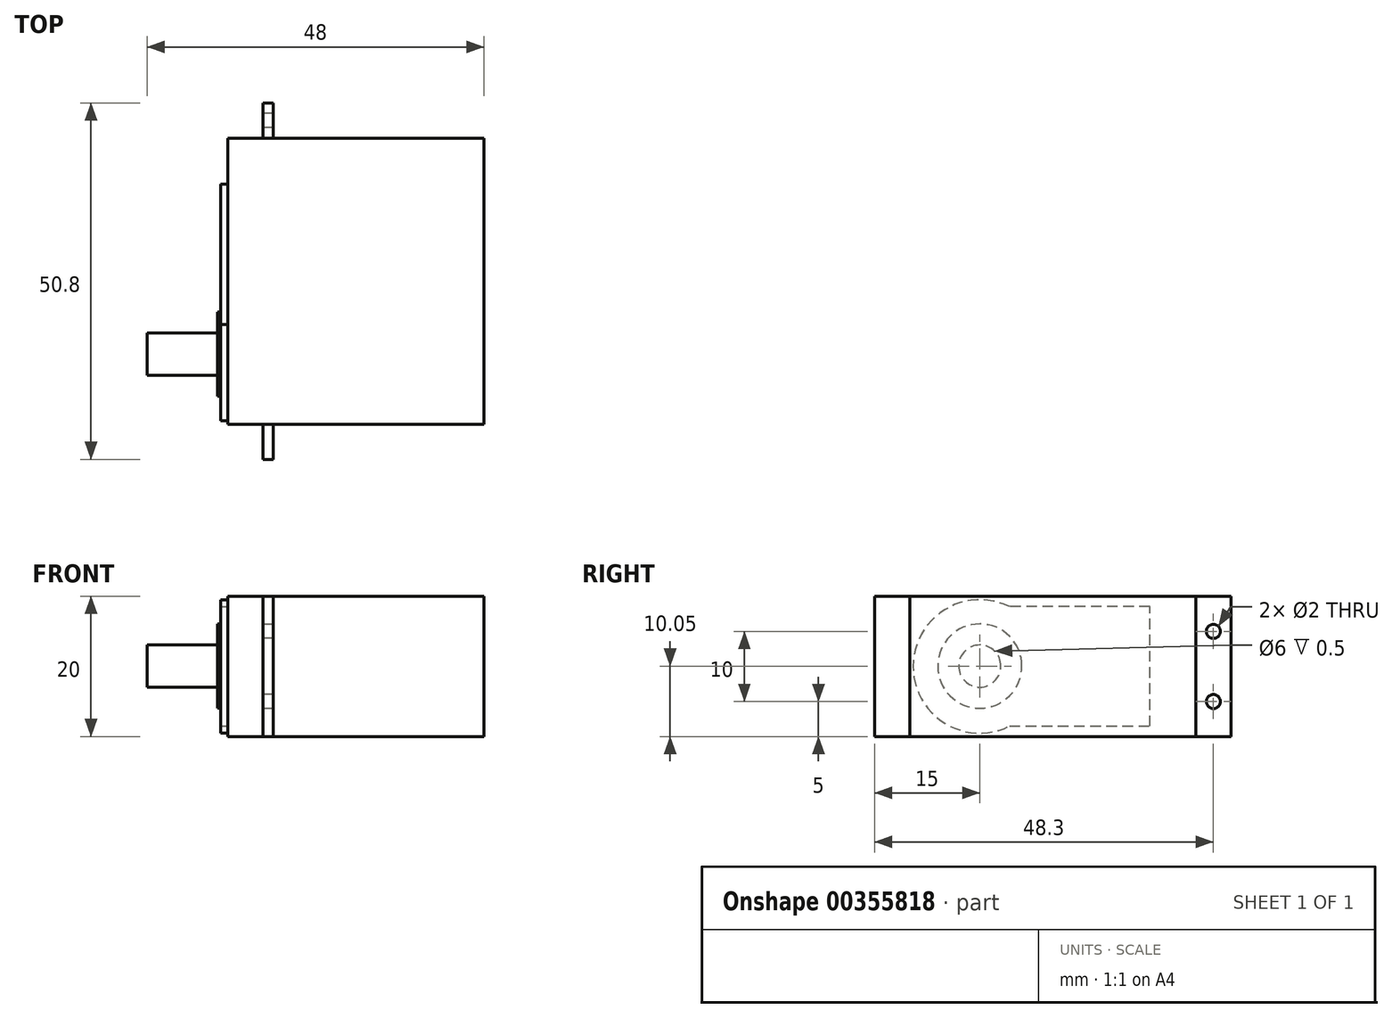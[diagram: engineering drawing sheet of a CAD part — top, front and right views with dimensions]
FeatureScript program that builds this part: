
annotation { "Feature Type Name" : "Feature", "Feature Type Description" : "" }
export const myFeature = defineFeature(function(context is Context, id is Id, definition is map)
    precondition{}
    {
        {
            var Q0;
            Q0=qCreatedBy(makeId("Front.planeOp"),FACE);
            var sketch = newSketch(context, id + "F0", { "sketchPlane" : qUnion([Q0])});
            skLineSegment(sketch, "E0.bottom", {"start": v(0, 0) * mm, "end": v(36.5, 0) * mm});
            skLineSegment(sketch, "E0.top", {"start": v(0, 20) * mm, "end": v(36.5, 20) * mm});
            skLineSegment(sketch, "E0.left", {"start": v(0, 0) * mm, "end": v(0, 20) * mm});
            skLineSegment(sketch, "E0.right", {"start": v(36.5, 0) * mm, "end": v(36.5, 20) * mm});
            skSolve(sketch);
        }
        {
            var Q0;
            Q0=qSketchRegion(id+"F0",true);
            extrude(context, id + "F1", {"entities" : qUnion([Q0]), "endBound" : BoundingType.SYMMETRIC, "depth" : 40.8 * mm});
        }
        {
            var Q0;
            Q0=qCreatedBy(makeId("Right.planeOp"),FACE);
            cPlane(context, id + "F2", {"entities" : qUnion([Q0]), "cplaneType" : CPlaneType.OFFSET, "offset" : 5 * mm, "width" : 150 * mm, "height" : 150 * mm});
        }
        {
            var Q0;
            Q0=qCreatedBy(id+"F2.planeOp",FACE);
            var sketch = newSketch(context, id + "F3", { "sketchPlane" : qUnion([Q0])});
            skLineSegment(sketch, "E1.0", {"start": v(-20.4, 0) * mm, "end": v(-20.4, 20) * mm});
            skLineSegment(sketch, "E2", {"start": v(-20.4, 0) * mm, "end": v(-25.4, 0) * mm});
            skLineSegment(sketch, "E3", {"start": v(-25.4, 0) * mm, "end": v(-25.4, 20) * mm});
            skLineSegment(sketch, "E4", {"start": v(-25.4, 20) * mm, "end": v(-20.4, 20) * mm});
            skSolve(sketch);
        }
        {
            var Q0;
            Q0=qSketchRegion(id+"F3",true);
            extrude(context, id + "F4", {"entities" : qUnion([Q0]), "depth" : 1.5 * mm});
        }
        {
            var Q0;
            Q0=makeQuery(id+"F4.opExtrude","SWEPT_BODY",BODY,{"disambiguationData":[OSD([sQuery(id+"F3.wireOp",EDGE,"E1.0"),sQuery(id+"F3.wireOp",EDGE,"E2"),sQuery(id+"F3.wireOp",EDGE,"E3"),sQuery(id+"F3.wireOp",EDGE,"E4")])]});
            var Q1;
            Q1=qCreatedBy(makeId("Front.planeOp"),FACE);
            mirror(context, id + "F5", {"entities" : qUnion([Q0]), "mirrorPlane" : qUnion([Q1])});
        }
        {
            var Q0;
            Q0=makeQuery(id+"F1.opExtrude","SWEPT_FACE",FACE,{"disambiguationData":[OSD([sQuery(id+"F0.wireOp",EDGE,"E0.left")])]});
            var sketch = newSketch(context, id + "F6", { "sketchPlane" : qUnion([Q0])});
            skArc(sketch, "E5", {"start": v(6.16, 1.5) * mm, "mid": v(19.9, 10) * mm, "end": v(6.16, 18.5) * mm});
            skPoint(sketch, "E5.centerSnap0", {"position": v(20.4, 10) * mm});
            skLineSegment(sketch, "E6", {"start": v(6.16, 1.5) * mm, "end": v(-13.84, 1.5) * mm});
            skLineSegment(sketch, "E7", {"start": v(-13.84, 1.5) * mm, "end": v(-13.84, 18.5) * mm});
            skLineSegment(sketch, "E8", {"start": v(-13.84, 18.5) * mm, "end": v(6.16, 18.5) * mm});
            skLineSegment(sketch, "E9", {"start": v(-45.44, 10) * mm, "end": v(35.03, 10) * mm, "construction": true});
            skPoint(sketch, "E9.startSnap0", {"position": v(-20.4, 10) * mm});
            skSolve(sketch);
        }
        {
            var Q0;
            Q0=qSketchRegion(id+"F6",true);
            extrude(context, id + "F7", {"entities" : qUnion([Q0]), "operationType" : NewBodyOperationType.ADD, "depth" : 1 * mm});
        }
        {
            var Q0;
            Q0=makeQuery(id+"F7.opExtrude","CAP_FACE",FACE,{"disambiguationData":[OSD([sQuery(id+"F6.wireOp",EDGE,"E5"),sQuery(id+"F6.wireOp",EDGE,"E6"),sQuery(id+"F6.wireOp",EDGE,"E7"),sQuery(id+"F6.wireOp",EDGE,"E8")])],"isStart":false});
            var sketch = newSketch(context, id + "F8", { "sketchPlane" : qUnion([Q0])});
            skCircle(sketch, "E10", {"center": v(10.4, 10.05) * mm, "radius": 6 * mm});
            skPoint(sketch, "E11.0.3.start.orphan", {"position": v(-13.84, 1.5) * mm});
            skPoint(sketch, "E11.0.1.end.orphan", {"position": v(-13.84, 18.5) * mm});
            skPoint(sketch, "E11.0.0.end.orphan", {"position": v(6.16, 18.5) * mm});
            skPoint(sketch, "E11.0.0.start.orphan", {"position": v(6.16, 1.5) * mm});
            skSolve(sketch);
        }
        {
            var Q0;
            Q0=qSketchRegion(id+"F8",true);
            extrude(context, id + "F9", {"entities" : qUnion([Q0]), "operationType" : NewBodyOperationType.ADD, "depth" : .5 * mm});
        }
        {
            var Q0;
            Q0=makeQuery(id+"F9.opExtrude","CAP_FACE",FACE,{"disambiguationData":[OSD([sQuery(id+"F8.wireOp",EDGE,"E10")])],"isStart":false});
            var sketch = newSketch(context, id + "F10", { "sketchPlane" : qUnion([Q0])});
            skCircle(sketch, "E12", {"center": v(10.4, 10.05) * mm, "radius": 3 * mm});
            skSolve(sketch);
        }
        {
            var Q0;
            Q0=qSketchRegion(id+"F10",true);
            extrude(context, id + "F11", {"entities" : qUnion([Q0]), "operationType" : NewBodyOperationType.REMOVE, "oppositeDirection" : true, "depth" : .5 * mm});
        }
        {
            var Q0;
            Q0=makeQuery(id+"F9.opExtrude","CAP_FACE",FACE,{"disambiguationData":[OSD([sQuery(id+"F8.wireOp",EDGE,"E10")])],"isStart":false});
            var sketch = newSketch(context, id + "F12", { "sketchPlane" : qUnion([Q0])});
            skCircle(sketch, "E13.0", {"center": v(10.4, 10.05) * mm, "radius": 3 * mm});
            skSolve(sketch);
        }
        {
            var Q0;
            Q0=qSketchRegion(id+"F12",true);
            extrude(context, id + "F13", {"entities" : qUnion([Q0]), "depth" : 10 * mm});
        }
        {
            var Q0;
            Q0=makeQuery(id+"F5.opPattern","COPY",FACE,{"derivedFrom":makeQuery(id+"F4.opExtrude","CAP_FACE",FACE,{"disambiguationData":[OSD([sQuery(id+"F3.wireOp",EDGE,"E1.0"),sQuery(id+"F3.wireOp",EDGE,"E2"),sQuery(id+"F3.wireOp",EDGE,"E3"),sQuery(id+"F3.wireOp",EDGE,"E4")])],"isStart":true}),"instanceName":"1"});
            var sketch = newSketch(context, id + "F14", { "sketchPlane" : qUnion([Q0])});
            skCircle(sketch, "E14", {"center": v(-22.9, 5) * mm, "radius": 1 * mm});
            skPoint(sketch, "E14.centerSnap0", {"position": v(-22.9, 0) * mm});
            skCircle(sketch, "E15", {"center": v(-22.9, 15) * mm, "radius": 1 * mm});
            skPoint(sketch, "E15.centerSnap0", {"position": v(-22.9, 20) * mm});
            skSolve(sketch);
        }
        {
            var Q0;
            Q0=qSketchRegion(id+"F14",true);
            extrude(context, id + "F15", {"entities" : qUnion([Q0]), "operationType" : NewBodyOperationType.REMOVE, "oppositeDirection" : true, "depth" : 25 * mm});
        }
    });
